# Revit family: WAEI-1000-1000
name_source: partatom
category: Generic Models
revit_build: Autodesk Revit 2017 (Build: 20171027_0315(x64)
units: mm (PartAtom-declared; Revit-internal decimal feet)

## family parameters
Always vertical = Yes
Can host rebar = No
Cut with Voids When Loaded = No
Host = Floor
Part Type = Normal
Room Calculation Point = No
Round Connector Dimension = Use Diameter
Shared = Yes

## types (5) — shared parameters
Belastbaarheid = 15 kN/m² volgens NEN-EN1991
Bevestiging = Frame gelaste ankers
C = 400 mm  [stored 1.31234 ft]
EI-1 = 30 minuten
EI-2 = 45 minuten
EW = 120 minuten
Model = WAEI
Speciale afmeting = Max. 1000 x 2000 mm
URL = https://www.gortergroup.com
brandwerende vulling = vulling
frame = geanodiseerd aluminium frame
vloerluik = geanodiseerd aluminium tranenplaat

## per-type parameters (varying)
| type | A | B | WAEI-600 t/m 1000 | Weight (kg) |
| WAEI-600-600 | 600 mm | 600 mm | Yes | 69 |
| WAEI-800-800 | 800 mm  [stored 2.62467 ft] | 800 mm  [stored 2.62467 ft] | Yes | 103 |
| WAEI-1000-1000 | 1000 mm  [stored 3.28084 ft] | 1000 mm  [stored 3.28084 ft] | Yes | 141 |
| WAEI-1000-1500 | 1500 mm  [stored 4.92126 ft] | 1000 mm  [stored 3.28084 ft] | No | 218 |
| WAEI-1000-2000 | 2000 mm  [stored 6.56168 ft] | 1000 mm  [stored 3.28084 ft] | No | 274 |

type visibility flags (boolean, named after types; folded from table):
- WAEI-600-600: Yes: (none)
- WAEI-800-800: Yes: (none)
- WAEI-1000-1000: Yes: (none)
- WAEI-1000-1500: Yes: WAEI-1000-1500
- WAEI-1000-2000: Yes: WAEI-1000-2000

note: [stored X ft] marks values corroborated as IEEE doubles in the binary element streams (Revit-internal decimal feet)

## geometry (parser evidence)
native form markers: Sweep x8
no freeform markers — native parametric forms only
